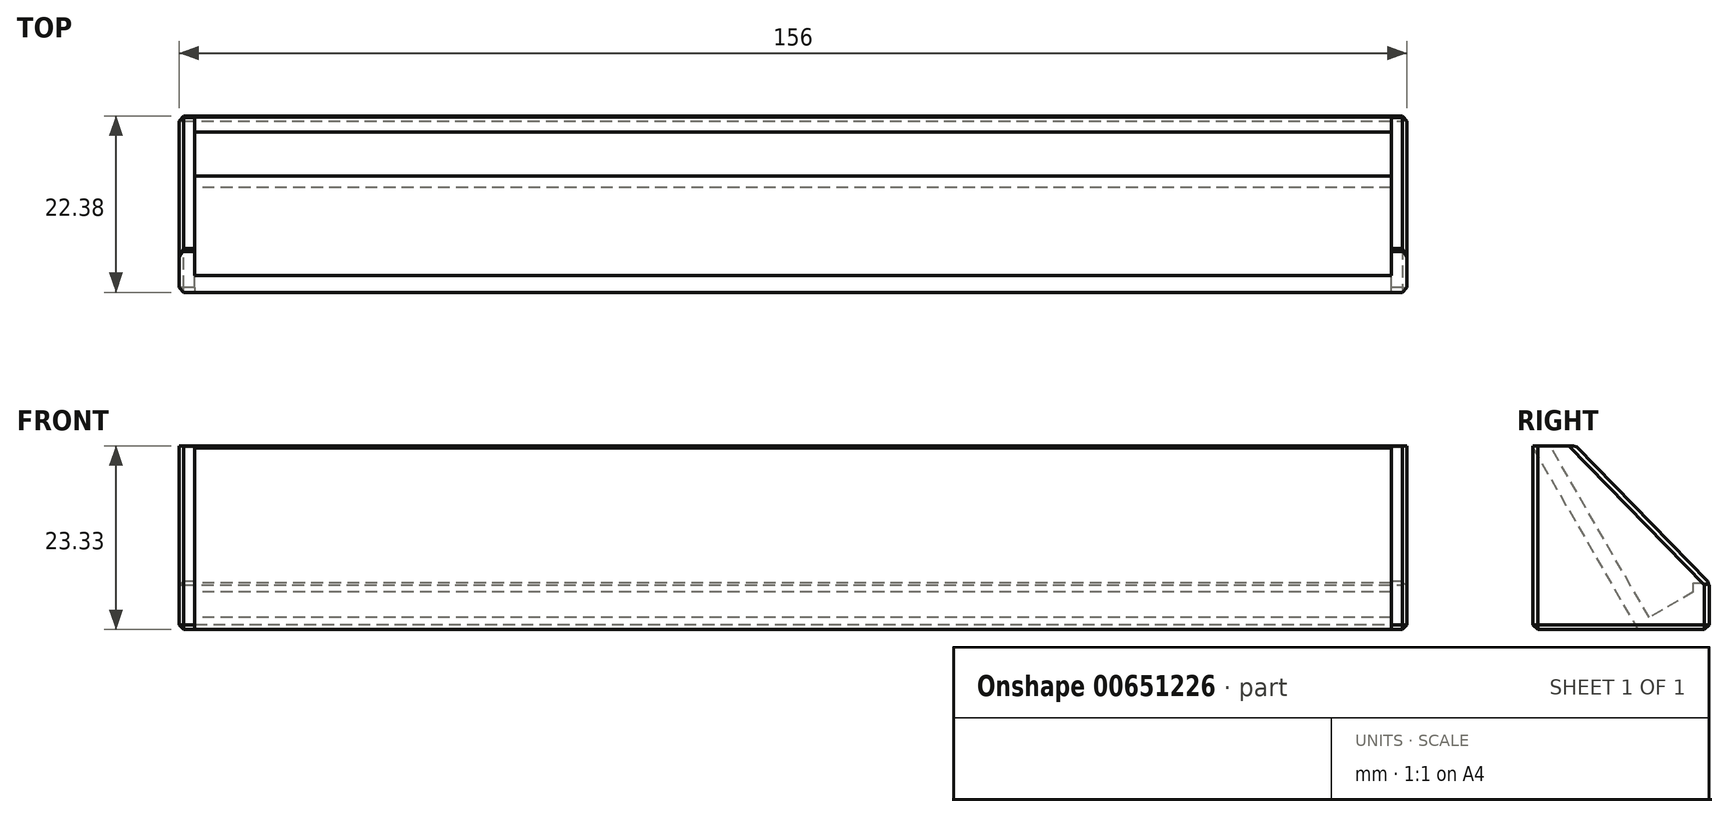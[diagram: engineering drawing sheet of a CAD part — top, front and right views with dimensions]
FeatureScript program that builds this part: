
annotation { "Feature Type Name" : "Feature", "Feature Type Description" : "" }
export const myFeature = defineFeature(function(context is Context, id is Id, definition is map)
    precondition{}
    {
        {
            var Q0;
            Q0=qCreatedBy(makeId("Right.planeOp"),FACE);
            var sketch = newSketch(context, id + "F0", { "sketchPlane" : qUnion([Q0])});
            skLineSegment(sketch, "E0", {"start": v(0, 0) * mm, "end": v(22.38, 0) * mm});
            skLineSegment(sketch, "E1", {"start": v(22.38, 0) * mm, "end": v(22.38, 5.9) * mm});
            skLineSegment(sketch, "E2", {"start": v(20.38, 4.75) * mm, "end": v(14.75, 1.5) * mm});
            skLineSegment(sketch, "E3", {"start": v(14.75, 1.5) * mm, "end": v(2, 23.58) * mm});
            skLineSegment(sketch, "E4", {"start": v(2, 23.58) * mm, "end": v(7.63, 26.83) * mm, "construction": true});
            skLineSegment(sketch, "E5", {"start": v(7.63, 26.83) * mm, "end": v(20.38, 4.75) * mm, "construction": true});
            skLineSegment(sketch, "E6", {"start": v(2, 26.83) * mm, "end": v(0, 26.83) * mm});
            skLineSegment(sketch, "E7", {"start": v(0, 26.83) * mm, "end": v(0, 0) * mm});
            skLineSegment(sketch, "E8", {"start": v(2, 26.83) * mm, "end": v(22.38, 5.9) * mm});
            skLineSegment(sketch, "E9", {"start": v(2, 23.58) * mm, "end": v(2, 29.83) * mm});
            skLineSegment(sketch, "E10", {"start": v(2, 29.83) * mm, "end": v(20.38, 29.83) * mm});
            skLineSegment(sketch, "E11", {"start": v(20.38, 4.75) * mm, "end": v(20.38, 29.83) * mm});
            skLineSegment(sketch, "E12", {"start": v(0, 23.05) * mm, "end": v(13.3, 0) * mm});
            skSolve(sketch);
        }
        {
            var Q0;
            {var subQ3=sQuery(id+"F0.wireOp",EDGE,"E1");Q0=makeQuery(id+"F0.imprint","IMPRINT",FACE,{"disambiguationData":[TD([[makeQuery(id+"F0.imprint","IMPRINT",EDGE,{"derivedFrom":subQ3}),1.0]])]});}
            extrude(context, id + "F1", {"entities" : qUnion([Q0]), "endBound" : BoundingType.SYMMETRIC, "depth" : (6 * 25 + 2) * mm, "offsetDistance" : 25 * mm});
        }
        {
            var Q0;
            {var subQ3=sQuery(id+"F0.wireOp",EDGE,"E12");Q0=makeQuery(id+"F0.imprint","IMPRINT",FACE,{"disambiguationData":[TD([[makeQuery(id+"F0.imprint","IMPRINT",EDGE,{"derivedFrom":subQ3}),-1.0]])]});}
            var Q1;
            {var subQ3=sQuery(id+"F0.wireOp",EDGE,"E1");Q1=makeQuery(id+"F0.imprint","IMPRINT",FACE,{"disambiguationData":[TD([[makeQuery(id+"F0.imprint","IMPRINT",EDGE,{"derivedFrom":subQ3}),1.0]])]});}
            var Q2;
            {var subQ6=sQuery(id+"F0.wireOp",EDGE,"E2");Q2=makeQuery(id+"F0.imprint","IMPRINT",FACE,{"disambiguationData":[TD([[makeQuery(id+"F0.imprint","IMPRINT",EDGE,{"derivedFrom":subQ6}),-1.0]])]});}
            extrude(context, id + "F2", {"entities" : qUnion([Q0, Q1, Q2]), "operationType" : NewBodyOperationType.ADD, "depth" : 78 * mm, "offsetDistance" : 25 * mm, "hasSecondDirection" : true, "secondDirectionOppositeDirection" : true, "secondDirectionDepth" : -76 * mm});
        }
        {
            var Q0;
            {var subQ3=sQuery(id+"F0.wireOp",EDGE,"E12");Q0=makeQuery(id+"F0.imprint","IMPRINT",FACE,{"disambiguationData":[TD([[makeQuery(id+"F0.imprint","IMPRINT",EDGE,{"derivedFrom":subQ3}),-1.0]])]});}
            var Q1;
            {var subQ6=sQuery(id+"F0.wireOp",EDGE,"E2");Q1=makeQuery(id+"F0.imprint","IMPRINT",FACE,{"disambiguationData":[TD([[makeQuery(id+"F0.imprint","IMPRINT",EDGE,{"derivedFrom":subQ6}),-1.0]])]});}
            var Q2;
            {var subQ3=sQuery(id+"F0.wireOp",EDGE,"E1");Q2=makeQuery(id+"F0.imprint","IMPRINT",FACE,{"disambiguationData":[TD([[makeQuery(id+"F0.imprint","IMPRINT",EDGE,{"derivedFrom":subQ3}),1.0]])]});}
            extrude(context, id + "F3", {"entities" : qUnion([Q0, Q1, Q2]), "operationType" : NewBodyOperationType.ADD, "oppositeDirection" : true, "depth" : 78 * mm, "offsetDistance" : 25 * mm, "hasSecondDirection" : true, "secondDirectionOppositeDirection" : false, "secondDirectionDepth" : -76 * mm});
        }
        {
            var Q0;
            Q0=qCreatedBy(makeId("Front.planeOp"),FACE);
            var sketch = newSketch(context, id + "F4", { "sketchPlane" : qUnion([Q0])});
            skLineSegment(sketch, "E13.bottom", {"start": v(78, 23.33) * mm, "end": v(-78, 23.33) * mm});
            skLineSegment(sketch, "E13.top", {"start": v(78, 26.83) * mm, "end": v(-78, 26.83) * mm});
            skLineSegment(sketch, "E13.left", {"start": v(78, 23.33) * mm, "end": v(78, 26.83) * mm});
            skLineSegment(sketch, "E13.right", {"start": v(-78, 23.33) * mm, "end": v(-78, 26.83) * mm});
            skSolve(sketch);
        }
        {
            var Q0;
            Q0 = qSketchRegion(id + "F4", true);
            extrude(context, id + "F5", {"entities" : qUnion([Q0]), "operationType" : NewBodyOperationType.REMOVE, "endBound" : BoundingType.THROUGH_ALL, "oppositeDirection" : true, "depth" : 25 * mm, "offsetDistance" : 25 * mm});
        }
        {
            var Q0;
            {var subQ0=sQuery(id+"F0.wireOp",EDGE,"E1");Q0=makeQuery(id+"F3.boolean.opBoolean","MERGE",FACE,{"derivedFrom":[makeQuery(id+"F2.boolean.opBoolean","MERGE",FACE,{"derivedFrom":[makeQuery(id+"F1.opExtrude","SWEPT_FACE",FACE,{"disambiguationData":[OSD([subQ0])]}),makeQuery(id+"F2.opExtrude","SWEPT_FACE",FACE,{"disambiguationData":[OSD([subQ0])]})]}),makeQuery(id+"F3.opExtrude","SWEPT_FACE",FACE,{"disambiguationData":[OSD([subQ0])]})]});}
            var sketch = newSketch(context, id + "F6", { "sketchPlane" : qUnion([Q0])});
            skLineSegment(sketch, "E14.bottom", {"start": v(-76, 5.9) * mm, "end": v(76, 5.9) * mm});
            skLineSegment(sketch, "E14.top", {"start": v(-76, 7.96) * mm, "end": v(76, 7.96) * mm});
            skLineSegment(sketch, "E14.left", {"start": v(-76, 5.9) * mm, "end": v(-76, 7.96) * mm});
            skLineSegment(sketch, "E14.right", {"start": v(76, 5.9) * mm, "end": v(76, 7.96) * mm});
            skSolve(sketch);
        }
        {
            var Q0;
            Q0 = qSketchRegion(id + "F6", true);
            var Q1;
            Q1=makeQuery(id+"F1.opExtrude","CAP_VERTEX",VERTEX,{"disambiguationData":[OSD([sQuery(id+"F0.wireOp",EDGE,"E8"),sQuery(id+"F0.wireOp",EDGE,"E11")])],"isStart":false});
            extrude(context, id + "F7", {"entities" : qUnion([Q0]), "operationType" : NewBodyOperationType.REMOVE, "endBound" : BoundingType.UP_TO_VERTEX, "oppositeDirection" : true, "depth" : 25 * mm, "endBoundEntityVertex" : qUnion([Q1]), "offsetDistance" : 25 * mm});
        }
        {
            var Q0;
            {var subQ0=sQuery(id+"F0.wireOp",EDGE,"E1");var subQ1=sQuery(id+"F0.wireOp",EDGE,"E0");Q0=makeQuery(id+"F3.boolean.opBoolean","MERGE",EDGE,{"derivedFrom":[makeQuery(id+"F2.boolean.opBoolean","MERGE",EDGE,{"derivedFrom":[makeQuery(id+"F1.opExtrude","SWEPT_EDGE",EDGE,{"disambiguationData":[OSD([subQ1,subQ0])]}),makeQuery(id+"F2.opExtrude","SWEPT_EDGE",EDGE,{"disambiguationData":[OSD([subQ1,subQ0])]})]}),makeQuery(id+"F3.opExtrude","SWEPT_EDGE",EDGE,{"disambiguationData":[OSD([subQ1,subQ0])]})]});}
            var Q1;
            Q1=makeQuery(id+"F2.opExtrude","CAP_EDGE",EDGE,{"disambiguationData":[OSD([sQuery(id+"F0.wireOp",EDGE,"E1")])],"isStart":false});
            var Q2;
            Q2=makeQuery(id+"F2.opExtrude","CAP_EDGE",EDGE,{"disambiguationData":[OSD([sQuery(id+"F0.wireOp",EDGE,"E0")])],"isStart":false});
            var Q3;
            Q3=makeQuery(id+"F3.opExtrude","CAP_EDGE",EDGE,{"disambiguationData":[OSD([sQuery(id+"F0.wireOp",EDGE,"E1")])],"isStart":false});
            var Q4;
            Q4=makeQuery(id+"F3.opExtrude","CAP_EDGE",EDGE,{"disambiguationData":[OSD([sQuery(id+"F0.wireOp",EDGE,"E0")])],"isStart":false});
            var Q5;
            Q5=makeQuery(id+"F3.opExtrude","SWEPT_EDGE",EDGE,{"disambiguationData":[OSD([sQuery(id+"F0.wireOp",EDGE,"E0"),sQuery(id+"F0.wireOp",EDGE,"E7")])]});
            var Q6;
            Q6=makeQuery(id+"F2.opExtrude","SWEPT_EDGE",EDGE,{"disambiguationData":[OSD([sQuery(id+"F0.wireOp",EDGE,"E0"),sQuery(id+"F0.wireOp",EDGE,"E7")])]});
            var Q7;
            Q7=makeQuery(id+"F5.boolean.opBoolean","COPY",EDGE,{"derivedFrom":makeQuery(id+"F5.opExtrude","CAP_EDGE",EDGE,{"disambiguationData":[OSD([sQuery(id+"F4.wireOp",EDGE,"E13.bottom")])],"isStart":true})});
            var Q8;
            Q8=makeQuery(id+"F3.opExtrude","CAP_EDGE",EDGE,{"disambiguationData":[OSD([sQuery(id+"F0.wireOp",EDGE,"E7")])],"isStart":false});
            var Q9;
            Q9=makeQuery(id+"F5.boolean.opBoolean","COPY",EDGE,{"derivedFrom":makeQuery(id+"F5.opExtrude","SWEPT_EDGE",EDGE,{"disambiguationData":[OSD([sQuery(id+"F4.wireOp",EDGE,"E13.bottom"),sQuery(id+"F4.wireOp",EDGE,"E13.right")])]})});
            var Q10;
            Q10=makeQuery(id+"F3.opExtrude","CAP_EDGE",EDGE,{"disambiguationData":[OSD([sQuery(id+"F0.wireOp",EDGE,"E8")])],"isStart":false});
            var Q11;
            {var subQ0=sQuery(id+"F0.wireOp",EDGE,"E8");Q11=makeQuery(id+"F5.boolean.opBoolean","INTERSECT",EDGE,{"disambiguationData":[OD(1.0)],"derivedFrom":[makeQuery(id+"F3.boolean.opBoolean","MERGE",FACE,{"derivedFrom":[makeQuery(id+"F2.boolean.opBoolean","MERGE",FACE,{"derivedFrom":[makeQuery(id+"F1.opExtrude","SWEPT_FACE",FACE,{"disambiguationData":[OSD([subQ0])]}),makeQuery(id+"F2.opExtrude","SWEPT_FACE",FACE,{"disambiguationData":[OSD([subQ0])]})]}),makeQuery(id+"F3.opExtrude","SWEPT_FACE",FACE,{"disambiguationData":[OSD([subQ0])]})]}),makeQuery(id+"F5.opExtrude","SWEPT_FACE",FACE,{"disambiguationData":[OSD([sQuery(id+"F4.wireOp",EDGE,"E13.bottom")])]})]});}
            var Q12;
            {var subQ0=sQuery(id+"F0.wireOp",EDGE,"E8");var subQ1=sQuery(id+"F0.wireOp",EDGE,"E1");Q12=makeQuery(id+"F7.boolean.opBoolean","SPLIT",EDGE,{"disambiguationData":[TD([makeQuery(id+"F7.opExtrude","SWEPT_FACE",FACE,{"disambiguationData":[OSD([sQuery(id+"F6.wireOp",EDGE,"E14.right")])]})])],"derivedFrom":makeQuery(id+"F3.boolean.opBoolean","MERGE",EDGE,{"derivedFrom":[makeQuery(id+"F2.boolean.opBoolean","MERGE",EDGE,{"derivedFrom":[makeQuery(id+"F1.opExtrude","SWEPT_EDGE",EDGE,{"disambiguationData":[OSD([subQ1,subQ0])]}),makeQuery(id+"F2.opExtrude","SWEPT_EDGE",EDGE,{"disambiguationData":[OSD([subQ1,subQ0])]})]}),makeQuery(id+"F3.opExtrude","SWEPT_EDGE",EDGE,{"disambiguationData":[OSD([subQ1,subQ0])]})]})});}
            var Q13;
            Q13=makeQuery(id+"F2.opExtrude","CAP_EDGE",EDGE,{"disambiguationData":[OSD([sQuery(id+"F0.wireOp",EDGE,"E8")])],"isStart":false});
            var Q14;
            {var subQ0=sQuery(id+"F0.wireOp",EDGE,"E8");Q14=makeQuery(id+"F5.boolean.opBoolean","INTERSECT",EDGE,{"disambiguationData":[OD(0.0)],"derivedFrom":[makeQuery(id+"F3.boolean.opBoolean","MERGE",FACE,{"derivedFrom":[makeQuery(id+"F2.boolean.opBoolean","MERGE",FACE,{"derivedFrom":[makeQuery(id+"F1.opExtrude","SWEPT_FACE",FACE,{"disambiguationData":[OSD([subQ0])]}),makeQuery(id+"F2.opExtrude","SWEPT_FACE",FACE,{"disambiguationData":[OSD([subQ0])]})]}),makeQuery(id+"F3.opExtrude","SWEPT_FACE",FACE,{"disambiguationData":[OSD([subQ0])]})]}),makeQuery(id+"F5.opExtrude","SWEPT_FACE",FACE,{"disambiguationData":[OSD([sQuery(id+"F4.wireOp",EDGE,"E13.bottom")])]})]});}
            var Q15;
            Q15=makeQuery(id+"F5.boolean.opBoolean","COPY",EDGE,{"derivedFrom":makeQuery(id+"F5.opExtrude","SWEPT_EDGE",EDGE,{"disambiguationData":[OSD([sQuery(id+"F4.wireOp",EDGE,"E13.bottom"),sQuery(id+"F4.wireOp",EDGE,"E13.left")])]})});
            var Q16;
            Q16=makeQuery(id+"F2.opExtrude","CAP_EDGE",EDGE,{"disambiguationData":[OSD([sQuery(id+"F0.wireOp",EDGE,"E7")])],"isStart":false});
            chamfer(context, id + "F8", {"entities" : qUnion([Q0, Q1, Q2, Q3, Q4, Q5, Q6, Q7, Q8, Q9, Q10, Q11, Q12, Q13, Q14, Q15, Q16]), "width" : .6 * mm, "tangentPropagation" : true});
        }
    });
